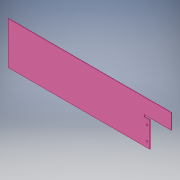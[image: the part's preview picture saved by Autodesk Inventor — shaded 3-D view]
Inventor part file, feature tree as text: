
AUTODESK INVENTOR PART (.ipt)
format: ipt  version: 2018 (Build 220112000, 112)  size: 117,248 bytes
history: native  units: mm
features: extrude x3, sketch x3
ambient origin geometry x8: Origin, YZ Plane, XZ Plane, XY Plane, X Axis, Y Axis, Z Axis, Center Point
bodies: Solid1 (feature_tree)
feature tree (6):
  extrude  "Extrusion1"  Depth=150.0mm
  extrude  "Extrusion3"  Depth=20.0mm
  extrude  "Extrusion4"  Depth=95.0mm
  sketch  "Sketch1"  dims[d0=500.0mm d1=150.0mm]
  sketch  "Sketch2"  dims[d2=1.6mm d3=0.0mm d6=20.0mm]
  sketch  "Sketch3"  dims[d7=60.0mm d10=5.0mm d11=5.0mm d12=50.0mm d13=20.0mm d14=1.6mm d15=0.0mm d16=54.0mm d17=1.6mm d18=95.0mm d19=0.0mm]
